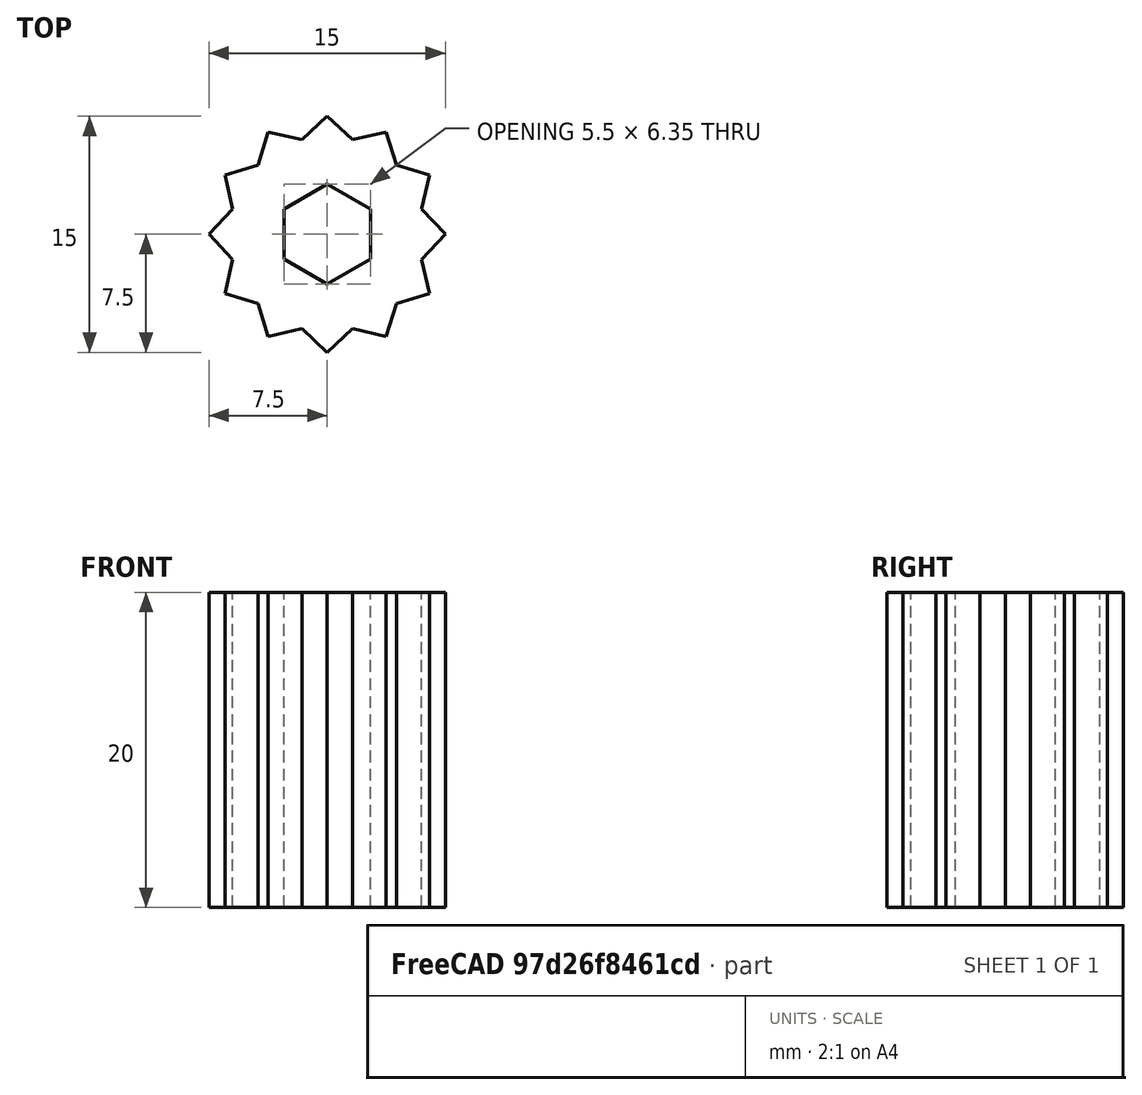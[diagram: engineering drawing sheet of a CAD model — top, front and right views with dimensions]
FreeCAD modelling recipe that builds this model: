
FCSTD DOCUMENT  (FreeCAD 0.19R24344 (Git))
Label: MicroManipulator_Handle2
License: Creative Commons Attribution-NonCommercial-ShareAlike
LicenseURL: http://creativecommons.org/licenses/by-nc-sa/4.0/
objects: Sketcher::SketchObject×1, PartDesign::Pad×1, PartDesign::Body×1
note: 4 computed .brp shape members not serialized (recipe doc carries the construction recipe); baked Part::Feature solids carry a one-line shape summary decoded from their .brp

FEATURE [Sketcher::SketchObject] Sketch
  FullyConstrained = true
  MapMode = 5
  Support = -> [XY_Plane]
  sketch-geometry (57):
    g0: LineSegment StartX=2.75 StartY=1.58771 StartZ=0 EndX=0 EndY=3.17543 EndZ=0
    g1: LineSegment StartX=0 StartY=3.17543 StartZ=0 EndX=-2.75 EndY=1.58771 EndZ=0
    g2: LineSegment StartX=-2.75 StartY=1.58771 StartZ=0 EndX=-2.75 EndY=-1.58771 EndZ=0
    g3: LineSegment StartX=-2.75 StartY=-1.58771 StartZ=0 EndX=0 EndY=-3.17543 EndZ=0
    g4: LineSegment StartX=0 StartY=-3.17543 StartZ=0 EndX=2.75 EndY=-1.58771 EndZ=0
    g5: LineSegment StartX=2.75 StartY=-1.58771 StartZ=0 EndX=2.75 EndY=1.58771 EndZ=0
    g6: Circle CenterX=0 CenterY=0 CenterZ=0 NormalX=0 NormalY=0 NormalZ=1 AngleXU=0 Radius=3.17543
    g7: LineSegment StartX=4.3923 StartY=4.3923 StartZ=0 EndX=1.6077 EndY=6 EndZ=0
    g8: LineSegment StartX=1.6077 StartY=6 StartZ=0 EndX=-1.6077 EndY=6 EndZ=0
    g9: LineSegment StartX=-1.6077 StartY=6 StartZ=0 EndX=-4.3923 EndY=4.3923 EndZ=0
    g10: LineSegment StartX=-4.3923 StartY=4.3923 StartZ=0 EndX=-6 EndY=1.6077 EndZ=0
    g11: LineSegment StartX=-6 StartY=1.6077 StartZ=0 EndX=-6 EndY=-1.6077 EndZ=0
    g12: LineSegment StartX=-6 StartY=-1.6077 StartZ=0 EndX=-4.3923 EndY=-4.3923 EndZ=0
    g13: LineSegment StartX=-4.3923 StartY=-4.3923 StartZ=0 EndX=-1.6077 EndY=-6 EndZ=0
    g14: LineSegment StartX=-1.6077 StartY=-6 StartZ=0 EndX=1.6077 EndY=-6 EndZ=0
    g15: LineSegment StartX=1.6077 StartY=-6 StartZ=0 EndX=4.3923 EndY=-4.3923 EndZ=0
    g16: LineSegment StartX=4.3923 StartY=-4.3923 StartZ=0 EndX=6 EndY=-1.6077 EndZ=0
    g17: LineSegment StartX=6 StartY=-1.6077 StartZ=0 EndX=6 EndY=1.6077 EndZ=0
    g18: LineSegment StartX=6 StartY=1.6077 StartZ=0 EndX=4.3923 EndY=4.3923 EndZ=0
    g19: Circle CenterX=0 CenterY=0 CenterZ=0 NormalX=0 NormalY=0 NormalZ=1 AngleXU=0 Radius=6.21166
    g20: LineSegment StartX=3.75 StartY=6.49519 StartZ=0 EndX=0 EndY=7.5 EndZ=0
    g21: LineSegment StartX=0 StartY=7.5 StartZ=0 EndX=-3.75 EndY=6.49519 EndZ=0
    g22: LineSegment StartX=-3.75 StartY=6.49519 StartZ=0 EndX=-6.49519 EndY=3.75 EndZ=0
    g23: LineSegment StartX=-6.49519 StartY=3.75 StartZ=0 EndX=-7.5 EndY=6.71e-14 EndZ=0
    g24: LineSegment StartX=-7.5 StartY=6.71e-14 StartZ=0 EndX=-6.49519 EndY=-3.75 EndZ=0
    g25: LineSegment StartX=-6.49519 StartY=-3.75 StartZ=0 EndX=-3.75 EndY=-6.49519 EndZ=0
    g26: LineSegment StartX=-3.75 StartY=-6.49519 StartZ=0 EndX=-4.49e-14 EndY=-7.5 EndZ=0
    g27: LineSegment StartX=-4.49e-14 StartY=-7.5 StartZ=0 EndX=3.75 EndY=-6.49519 EndZ=0
    g28: LineSegment StartX=3.75 StartY=-6.49519 StartZ=0 EndX=6.49519 EndY=-3.75 EndZ=0
    g29: LineSegment StartX=6.49519 StartY=-3.75 StartZ=0 EndX=7.5 EndY=-2.22e-14 EndZ=0
    g30: LineSegment StartX=7.5 StartY=-2.22e-14 StartZ=0 EndX=6.49519 EndY=3.75 EndZ=0
    g31: LineSegment StartX=6.49519 StartY=3.75 StartZ=0 EndX=3.75 EndY=6.49519 EndZ=0
    g32: Circle CenterX=0 CenterY=0 CenterZ=0 NormalX=0 NormalY=0 NormalZ=1 AngleXU=0 Radius=7.5
    g33: LineSegment StartX=-3.75 StartY=6.49519 StartZ=0 EndX=-1.6077 EndY=6 EndZ=0
    g34: LineSegment StartX=-1.6077 StartY=6 StartZ=0 EndX=0 EndY=7.5 EndZ=0
    g35: LineSegment StartX=0 StartY=7.5 StartZ=0 EndX=1.6077 EndY=6 EndZ=0
    g36: LineSegment StartX=1.6077 StartY=6 StartZ=0 EndX=3.75 EndY=6.49519 EndZ=0
    g37: LineSegment StartX=3.75 StartY=6.49519 StartZ=0 EndX=4.3923 EndY=4.3923 EndZ=0
    g38: LineSegment StartX=4.3923 StartY=4.3923 StartZ=0 EndX=6.49519 EndY=3.75 EndZ=0
    g39: LineSegment StartX=6.49519 StartY=3.75 StartZ=0 EndX=6 EndY=1.6077 EndZ=0
    g40: LineSegment StartX=6 StartY=1.6077 StartZ=0 EndX=7.5 EndY=-2.22e-14 EndZ=0
    g41: LineSegment StartX=7.5 StartY=-2.22e-14 StartZ=0 EndX=6 EndY=-1.6077 EndZ=0
    g42: LineSegment StartX=6 StartY=-1.6077 StartZ=0 EndX=6.49519 EndY=-3.75 EndZ=0
    g43: LineSegment StartX=6.49519 StartY=-3.75 StartZ=0 EndX=4.3923 EndY=-4.3923 EndZ=0
    g44: LineSegment StartX=4.3923 StartY=-4.3923 StartZ=0 EndX=3.75 EndY=-6.49519 EndZ=0
    g45: LineSegment StartX=3.75 StartY=-6.49519 StartZ=0 EndX=1.6077 EndY=-6 EndZ=0
    g46: LineSegment StartX=1.6077 StartY=-6 StartZ=0 EndX=-4.49e-14 EndY=-7.5 EndZ=0
    g47: LineSegment StartX=-4.49e-14 StartY=-7.5 StartZ=0 EndX=-1.6077 EndY=-6 EndZ=0
    g48: LineSegment StartX=-1.6077 StartY=-6 StartZ=0 EndX=-3.75 EndY=-6.49519 EndZ=0
    g49: LineSegment StartX=-3.75 StartY=-6.49519 StartZ=0 EndX=-4.3923 EndY=-4.3923 EndZ=0
    g50: LineSegment StartX=-4.3923 StartY=-4.3923 StartZ=0 EndX=-6.49519 EndY=-3.75 EndZ=0
    g51: LineSegment StartX=-6.49519 StartY=-3.75 StartZ=0 EndX=-6 EndY=-1.6077 EndZ=0
    g52: LineSegment StartX=-6 StartY=-1.6077 StartZ=0 EndX=-7.5 EndY=6.71e-14 EndZ=0
    g53: LineSegment StartX=-7.5 StartY=6.71e-14 StartZ=0 EndX=-6 EndY=1.6077 EndZ=0
    g54: LineSegment StartX=-6 StartY=1.6077 StartZ=0 EndX=-6.49519 EndY=3.75 EndZ=0
    g55: LineSegment StartX=-6.49519 StartY=3.75 StartZ=0 EndX=-4.3923 EndY=4.3923 EndZ=0
    g56: LineSegment StartX=-4.3923 StartY=4.3923 StartZ=0 EndX=-3.75 EndY=6.49519 EndZ=0
  constraints (120):
    c: Coincident(g0,g1)
    c: Coincident(g1,g2)
    c: Coincident(g2,g3)
    c: Coincident(g3,g4)
    c: Coincident(g4,g5)
    c: Coincident(g5,g0)
    c: Equal(g0, g1-g5) x5
    c: PointOnObject(g0,g6)
    c: PointOnObject(g1,g6)
    c: PointOnObject(g2,g6)
    c: PointOnObject(g3,g6)
    c: PointOnObject(g4,g6)
    c: PointOnObject(g5,g6)
    c: Coincident(g6,g-1)
    c: Vertical(g2)
    c: DistanceX(g1,g0) = 5.5
    c: Coincident(g7,g8)
    c: Coincident(g8,g9)
    c: Coincident(g9,g10)
    c: Coincident(g10,g11)
    c: Coincident(g11,g12)
    c: Coincident(g12,g13)
    c: Coincident(g13,g14)
    c: Coincident(g14,g15)
    c: Coincident(g15,g16)
    c: Coincident(g16,g17)
    c: Coincident(g17,g18)
    c: Coincident(g18,g7)
    c: Equal(g7, g8-g18) x11
    c: PointOnObject(g7,g19)
    c: PointOnObject(g8,g19)
    c: PointOnObject(g9,g19)
    c: PointOnObject(g10,g19)
    c: PointOnObject(g11,g19)
    c: PointOnObject(g12,g19)
    c: PointOnObject(g13,g19)
    c: PointOnObject(g14,g19)
    c: PointOnObject(g15,g19)
    c: PointOnObject(g16,g19)
    c: PointOnObject(g17,g19)
    c: PointOnObject(g18,g19)
    c: Coincident(g19,g-1)
    c: Coincident(g20,g21)
    c: Coincident(g21,g22)
    c: Coincident(g22,g23)
    c: Coincident(g23,g24)
    c: Coincident(g24,g25)
    c: Coincident(g25,g26)
    c: Coincident(g26,g27)
    c: Coincident(g27,g28)
    c: Coincident(g28,g29)
    c: Coincident(g29,g30)
    c: Coincident(g30,g31)
    c: Coincident(g31,g20)
    c: Equal(g20, g21-g31) x11
    c: PointOnObject(g20,g32)
    c: PointOnObject(g21,g32)
    c: PointOnObject(g22,g32)
    c: PointOnObject(g23,g32)
    c: PointOnObject(g24,g32)
    c: PointOnObject(g25,g32)
    c: PointOnObject(g26,g32)
    c: PointOnObject(g27,g32)
    c: PointOnObject(g28,g32)
    c: PointOnObject(g29,g32)
    c: PointOnObject(g30,g32)
    c: PointOnObject(g31,g32)
    c: Coincident(g32,g-1)
    c: Vertical(g17)
    c: DistanceX(g10,g17) = 12
    c: PointOnObject(g20,g-2)
    c: DistanceX(g23,g29) = 15
    c: Coincident(g21,g33)
    c: Coincident(g33,g8)
    c: Coincident(g33,g34)
    c: Coincident(g34,g20)
    c: Coincident(g34,g35)
    c: Coincident(g35,g7)
    c: Coincident(g35,g36)
    c: Coincident(g36,g20)
    c: Coincident(g36,g37)
    c: Coincident(g37,g7)
    c: Coincident(g37,g38)
    c: Coincident(g38,g30)
    c: Coincident(g38,g39)
    c: Coincident(g39,g17)
    c: Coincident(g39,g40)
    c: Coincident(g40,g29)
    c: Coincident(g40,g41)
    c: Coincident(g41,g16)
    c: Coincident(g41,g42)
    c: Coincident(g42,g28)
    c: Coincident(g42,g43)
    c: Coincident(g43,g15)
    c: Coincident(g43,g44)
    c: Coincident(g44,g27)
    c: Coincident(g44,g45)
    c: Coincident(g45,g14)
    c: Coincident(g45,g46)
    c: Coincident(g46,g26)
    c: Coincident(g46,g47)
    c: Coincident(g47,g13)
    c: Coincident(g47,g48)
    c: Coincident(g48,g25)
    c: Coincident(g48,g49)
    c: Coincident(g49,g12)
    c: Coincident(g49,g50)
    c: Coincident(g50,g24)
    c: Coincident(g50,g51)
    c: Coincident(g51,g11)
    c: Coincident(g51,g52)
    c: Coincident(g52,g23)
    c: Coincident(g52,g53)
    c: Coincident(g53,g10)
    c: Coincident(g53,g54)
    c: Coincident(g54,g22)
    c: Coincident(g54,g55)
    c: Coincident(g55,g9)
    c: Coincident(g55,g56)
    c: Coincident(g56,g33)
FEATURE [PartDesign::Pad] Pad
  Direction = (1,1,1)
  Length = 20
  Length2 = 100
  Profile = -> Sketch
  Type = 0
FEATURE [PartDesign::Body] Body
  Group = -> [Sketch,Pad]
  Origin = -> Origin
  Tip = -> Pad
